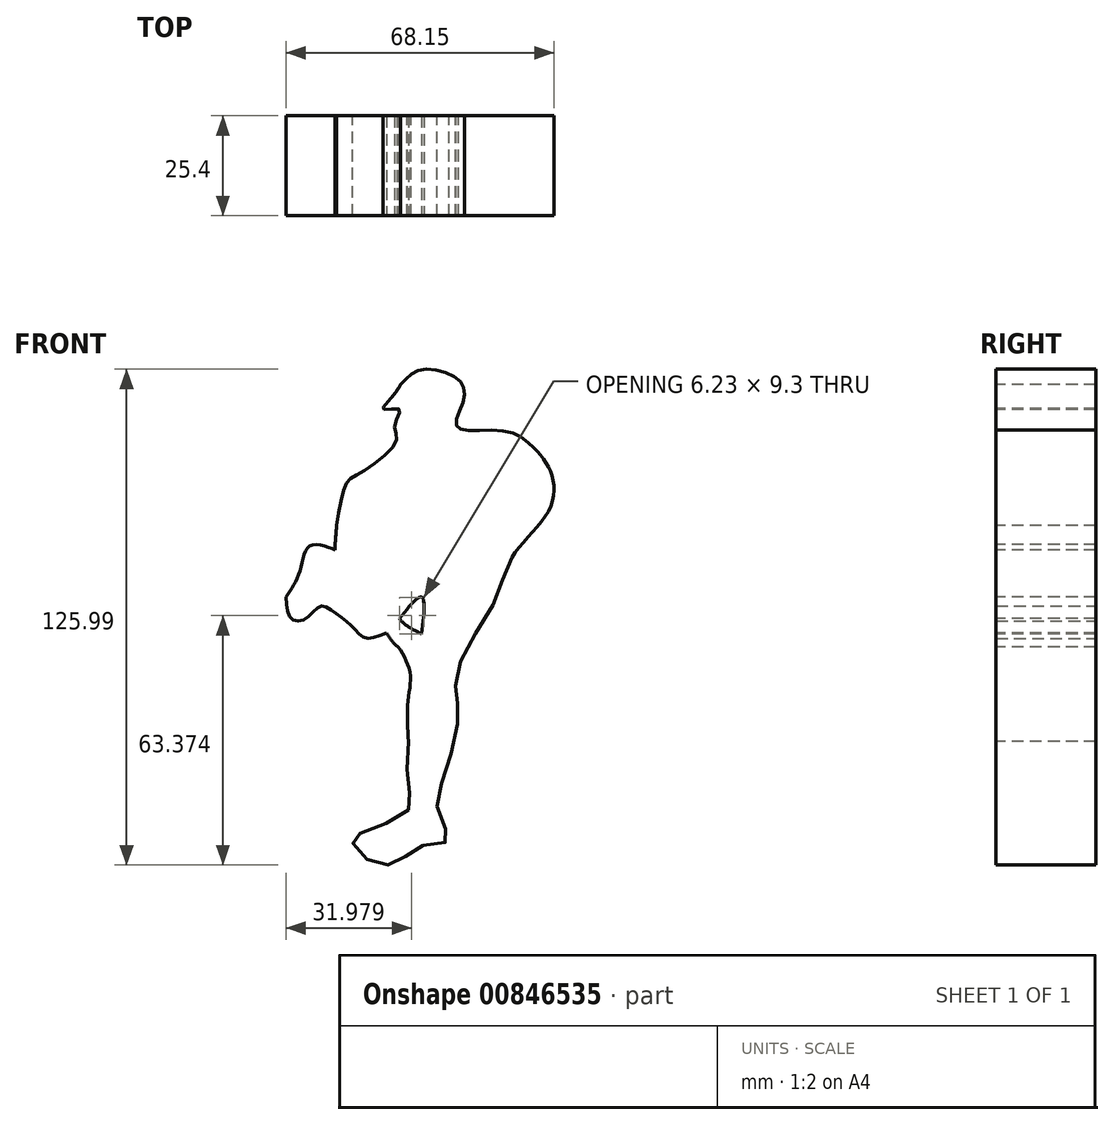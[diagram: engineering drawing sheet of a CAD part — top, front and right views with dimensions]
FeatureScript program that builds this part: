
annotation { "Feature Type Name" : "Feature", "Feature Type Description" : "" }
export const myFeature = defineFeature(function(context is Context, id is Id, definition is map)
    precondition{}
    {
        {
            var Q0;
            Q0=qCreatedBy(makeId("Front.planeOp"),FACE);
            var sketch = newSketch(context, id + "F0", { "sketchPlane" : qUnion([Q0])});
            skFitSpline(sketch, "E0", {"points": [v(-21.6, 18.19) * mm, v(-18.97, 29.07) * mm, v(-15.4, 31.7) * mm, v(-6.4, 39.77) * mm, v(-6.9, 43.62) * mm, v(-5.63, 47.72) * mm, v(-9.74, 47.72) * mm, v(-7.53, 50.88) * mm, v(-5.32, 54.03) * mm, v(-5.97, 52.7) * mm], "startDerivative": vector(12.68, 80.12) * mm, "endDerivative": vector(-16.63, -32.72) * mm});
            skFitSpline(sketch, "E1", {"points": [v(-21.6, 18.19) * mm, v(-21.6, 6.72) * mm, v(-17.6, 0) * mm, v(-10.66, -6.41) * mm, v(-5.97, -12.6) * mm, v(-2.03, -13.36) * mm, v(0, -16.74) * mm, v(3.6, -18.99) * mm, v(5.85, -19.93) * mm, v(6.98, -17.3) * mm, v(2.29, -10.73) * mm, v(-5.63, -5.48) * mm, v(-7.66, 1.66) * mm, v(-10.66, 5.6) * mm, v(-10.48, 11.04) * mm, v(-5.97, 18.19) * mm, v(-5.63, 21.17) * mm], "startDerivative": vector(-13.18, -142.27) * mm, "endDerivative": vector(-5.68, 61.8) * mm});
            skFitSpline(sketch, "E2", {"points": [v(-34.5, 0) * mm, v(-30.93, 6.72) * mm, v(-27.74, 13.3) * mm, v(-22.02, 12) * mm, v(-22.02, 12) * mm], "startDerivative": vector(12.04, 17.3) * mm, "endDerivative": vector(-0.44, 0.9) * mm});
            skFitSpline(sketch, "E3", {"points": [v(-34.5, 0) * mm, v(-33.1, -5.48) * mm, v(-29.43, -5.48) * mm, v(-25.68, -2.29) * mm, v(-21.97, -3.98) * mm, v(-17.6, -7.54) * mm, v(-14.42, -10.36) * mm, v(-8.9, -9.14) * mm], "startDerivative": vector(2.68, -43.44) * mm, "endDerivative": vector(39.34, 15.88) * mm});
            skFitSpline(sketch, "E4", {"points": [v(-5.97, -12.6) * mm, v(-2.97, -19.18) * mm, v(-3.53, -27.25) * mm, v(-3.34, -36.63) * mm], "startDerivative": vector(12.67, -20.25) * mm, "endDerivative": vector(1.95, -26.62) * mm});
            skFitSpline(sketch, "E5", {"points": [v(-3.34, -36.63) * mm, v(-3.34, -48.6) * mm, v(-3.34, -53.97) * mm, v(-14.68, -59.65) * mm, v(-17.6, -61.86) * mm, v(-12.78, -67.23) * mm, v(-5.97, -67.23) * mm, v(0, -63.12) * mm, v(6.79, -61.86) * mm, v(4.26, -54.92) * mm, v(5.84, -45.13) * mm, v(9.31, -29.98) * mm, v(8.68, -24.93) * mm, v(10.26, -15.47) * mm, v(19.1, 0) * mm, v(22.88, 10.1) * mm, v(32.35, 22.1) * mm, v(32.98, 31.25) * mm, v(28.56, 37.87) * mm, v(20.36, 42.3) * mm, v(9, 43.24) * mm, v(10.57, 49.87) * mm, v(9.31, 55.23) * mm, v(0, 57.76) * mm, v(-5.32, 54.03) * mm], "startDerivative": vector(-17.22, -270.12) * mm, "endDerivative": vector(-122.75, -137.58) * mm});
            skFitSpline(sketch, "E6", {"points": [v(0, -9.37) * mm, v(0, 0) * mm, v(-5.63, -5.48) * mm], "startDerivative": vector(3.08, 25.63) * mm, "endDerivative": vector(-14.6, -18.49) * mm});
            skFitSpline(sketch, "E7", {"points": [v(22.88, 10.1) * mm, v(16.25, 10.1) * mm, v(15.3, 14.09) * mm, v(19.1, 27.46) * mm, v(22.88, 31.25) * mm, v(27.62, 29.04) * mm, v(22.88, 17.67) * mm, v(25.4, 18) * mm, v(27.3, 22.72) * mm, v(27.62, 25.25) * mm, v(27.62, 27.14) * mm], "startDerivative": vector(-72.34, -10.61) * mm, "endDerivative": vector(-0.88, 31.97) * mm});
            skFitSpline(sketch, "E8", {"points": [v(-12.78, 27.46) * mm, v(-5.63, 22.72) * mm, v(-5.63, 21.17) * mm], "startDerivative": vector(13.76, -7.3) * mm, "endDerivative": vector(-1.52, -4.97) * mm});
            skFitSpline(sketch, "E9", {"points": [v(0, -52.7) * mm, v(0, -47.03) * mm, v(3.95, -33.47) * mm, v(5.85, -19.93) * mm], "startDerivative": vector(-2.45, 20.95) * mm, "endDerivative": vector(2.8, 35.18) * mm});
            skFitSpline(sketch, "E10", {"points": [v(27.62, 29.04) * mm, v(28.56, 37.87) * mm], "startDerivative": vector(0.95, 8.84) * mm, "endDerivative": vector(0.95, 8.84) * mm});
            skSolve(sketch);
        }
        {
            var Q0;
            Q0 = qSketchRegion(id + "F0", true);
            extrude(context, id + "F1", {"entities" : qUnion([Q0]), "oppositeDirection" : true, "depth" : 25.4 * mm, "offsetDistance" : 25.4 * mm});
        }
    });
